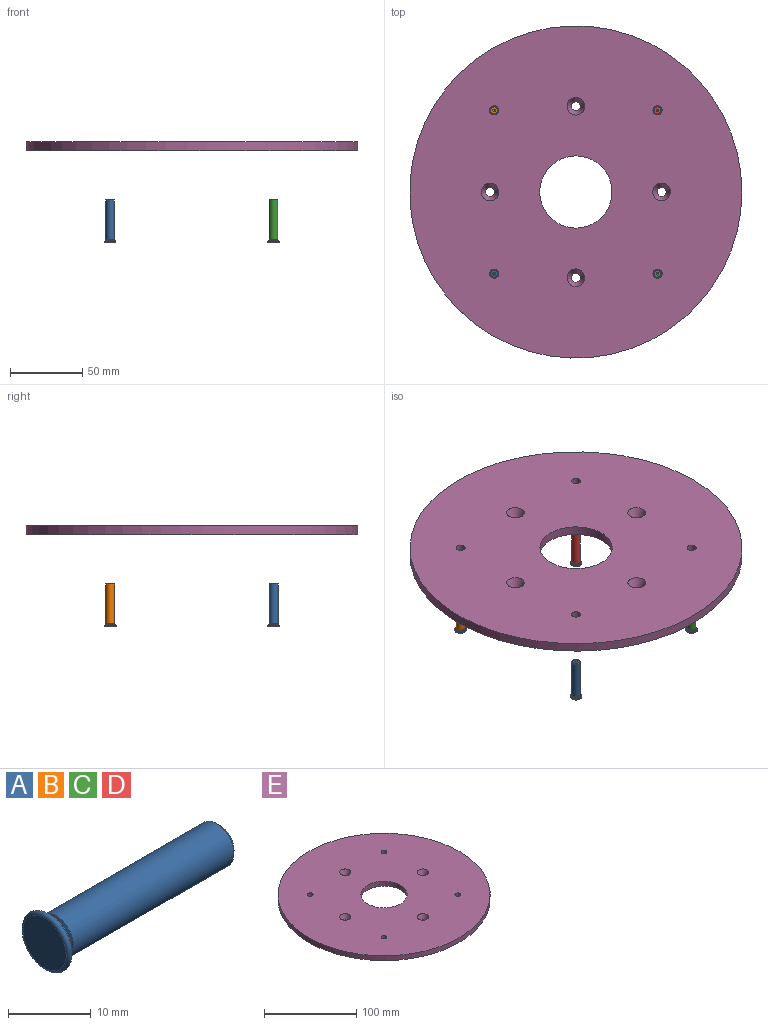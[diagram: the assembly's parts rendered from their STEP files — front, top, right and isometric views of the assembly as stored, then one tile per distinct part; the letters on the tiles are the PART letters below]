
ASSEMBLY  parts=5 mates=4
PART A: 13 faces, bbox 30x8.9x8.9 mm
  f0: cone r=0.45mm half-angle=60deg, axis (1,0,0), area 2.9mm2, adj f1
  f1: plane 4.77x4.77mm, normal (1,0,0), area 15.3mm2, adj f0,f2
  f2: cone r=2.69mm half-angle=45deg, axis (-1,0,0), area 14.7mm2, adj f1,f3
  f3: cylinder r=3mm len=27.39mm, axis (-1,0,0), area 516.2mm2, adj f2,f4
  f4: cone r=2.85mm half-angle=63.4deg, axis (1,0,0), area 6mm2, adj f3,f5
  f5: torus R=2.83mm, axis (-1,0,0), area 2.7mm2, adj f4,f6
  f6: cone r=2.85mm half-angle=63.4deg, axis (-1,0,0), area 6mm2, adj f5,f7
  f7: cylinder r=3mm len=6mm, axis (-1,0,0), area 6mm2, adj f6,f8
  f8: plane 6.97x6.97mm, normal (1,0,0), area 9.9mm2, adj f7,f9
  f9: cylinder r=3.48mm len=6.97mm, axis (1,0,0), area 9mm2, adj f8,f12
  f10: plane 7.38x7.38mm, normal (-1,0,0), area 42.8mm2, adj f11
  f11: torus R=3.69mm, axis (-1,0,0), area 32mm2, adj f10,f12
  f12: plane 7.38x7.38mm, normal (1,0,0), area 4.6mm2, adj f9,f11
PART B: same geometry as A
PART C: same geometry as A
PART D: same geometry as A
PART E: 16 faces, bbox 230x230x6.4 mm
  f0: cylinder r=3.15mm len=6.35mm, axis (0,0,1), area 125.7mm2, adj f11,f12
  f1: cylinder r=3.15mm len=6.35mm, axis (0,0,1), area 125.7mm2, adj f11,f12
  f2: cylinder r=3.15mm len=6.35mm, axis (0,0,1), area 125.7mm2, adj f11,f12
  f3: cylinder r=3.17mm len=6.35mm, axis (0,0,1), area 1.1mm2, adj f4,f12
  f4: cone r=3.17mm half-angle=25deg, axis (0,0,1), area 202.6mm2, adj f3,f11
  f5: cylinder r=3.17mm len=6.35mm, axis (0,0,1), area 1.1mm2, adj f6,f12
  f6: cone r=3.17mm half-angle=25deg, axis (0,0,1), area 202.6mm2, adj f5,f11
  f7: cylinder r=3.17mm len=6.35mm, axis (0,0,1), area 1.1mm2, adj f8,f12
  f8: cone r=3.17mm half-angle=25deg, axis (0,0,1), area 202.6mm2, adj f7,f11
  f9: cylinder r=25mm len=50mm, axis (0,0,-1), area 997.5mm2, adj f11,f12
  f10: cylinder r=115mm len=230mm, axis (0,0,-1), area 4588.3mm2, adj f11,f12
  f11: plane 230x230mm, normal (0,0,1), area 38990.2mm2, adj f0,f1,f2,f4,f6,f8,f9,f10
  f12: plane 230x230mm, normal (0,0,-1), area 39332.7mm2, adj f0,f1,f2,f3,f5,f7,f9,f10
  f13: cylinder r=3.17mm len=6.35mm, axis (0,0,1), area 1.1mm2, adj f12,f14
  f14: cone r=3.17mm half-angle=25deg, axis (0,0,1), area 202.6mm2, adj f11,f13
  f15: cylinder r=3.15mm len=6.35mm, axis (0,0,1), area 125.7mm2, adj f11,f12
PLACE A rot(axis=(0,-1,0),90deg) t=(-120.03,-80.44,-50.84)mm
PLACE B rot(axis=(0,-1,0),90deg) t=(-120.03,32.7,-50.84)mm
PLACE C rot(axis=(0,-1,0),90deg) t=(-6.9,-80.44,-50.84)mm
PLACE D rot(axis=(0,-1,0),90deg) t=(-6.9,32.7,-50.84)mm
PLACE E t=(-63.47,-23.87,12.66)mm
MATE cylindrical A.f2 <-> E.f1  axis (0,0,-1) through (-120.03,-80.44,-50.84)mm
MATE cylindrical B.f2 <-> E.f2  axis (0,0,-1) through (-120.03,32.7,-50.84)mm
MATE cylindrical C.f2 <-> E.f0  axis (0,0,-1) through (-6.9,-80.44,-50.84)mm
MATE cylindrical D.f2 <-> E.f15  axis (0,0,-1) through (-6.9,32.7,-50.84)mm
